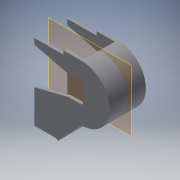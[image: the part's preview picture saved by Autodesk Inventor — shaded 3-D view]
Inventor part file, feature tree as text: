
AUTODESK INVENTOR PART (.ipt)
format: ipt  version: 2016 (Build 200138000, 138)  size: 218,112 bytes
history: native  units: mm
features: sketch x7, extrude x6, projected_geometry x5, mirror x2, revolve x1, plane x1
ambient origin geometry x8: Origin, YZ Plane, XZ Plane, XY Plane, X Axis, Y Axis, Z Axis, Center Point
bodies: Solid1 (feature_tree)
feature tree (22):
  revolve  "Revolution1"  [1 undecoded]
  extrude  "Extrusion1"  Depth=58.0mm
  extrude  "Extrusion2"  Depth=42.0mm
  plane  "Work Plane1"
  mirror  "Mirror1"
  extrude  "Extrusion3"  Depth=110.0mm
  extrude  "Extrusion4"  Depth=110.0mm TaperAngle=0.0deg
  extrude  "Extrusion5"  Depth=3.0mm
  mirror  "Mirror2"
  extrude  "Extrusion6"  Depth=84.0mm
  sketch  "Sketch1"  dims[d2=7.0mm d3=65.0mm]
  sketch  "Sketch2"  dims[d4=180.0deg d5=58.0mm]
  projected_geometry  "Projected Loop1"
  sketch  "Sketch3"  dims[d6=84.0mm d7=42.0mm]
  projected_geometry  "Projected Loop2"
  sketch  "Sketch4"  dims[d8=110.0mm d9=0.0mm d11=30.0mm]
  projected_geometry  "Projected Loop3"
  sketch  "Sketch5"  dims[d13=2.443461mm d14=110.0mm d15=0.0mm]
  projected_geometry  "Projected Loop4"
  sketch  "Sketch6"  dims[d17=21.0mm d18=3.0mm]
  projected_geometry  "Projected Loop5"
  sketch  "Sketch7"  dims[d19=110.0mm d20=0.0mm d21=80.0mm d22=84.0mm d23=0.0mm d24=7.0mm d25=0.0mm d26=68.0mm d27=9.0mm d28=84.0mm d29=0.0mm]
note: 1 required parameter value undecoded (feature->parameter linkage not recoverable at this tier; creation-order binding heuristic only, values carry confidence <= 0.55)
